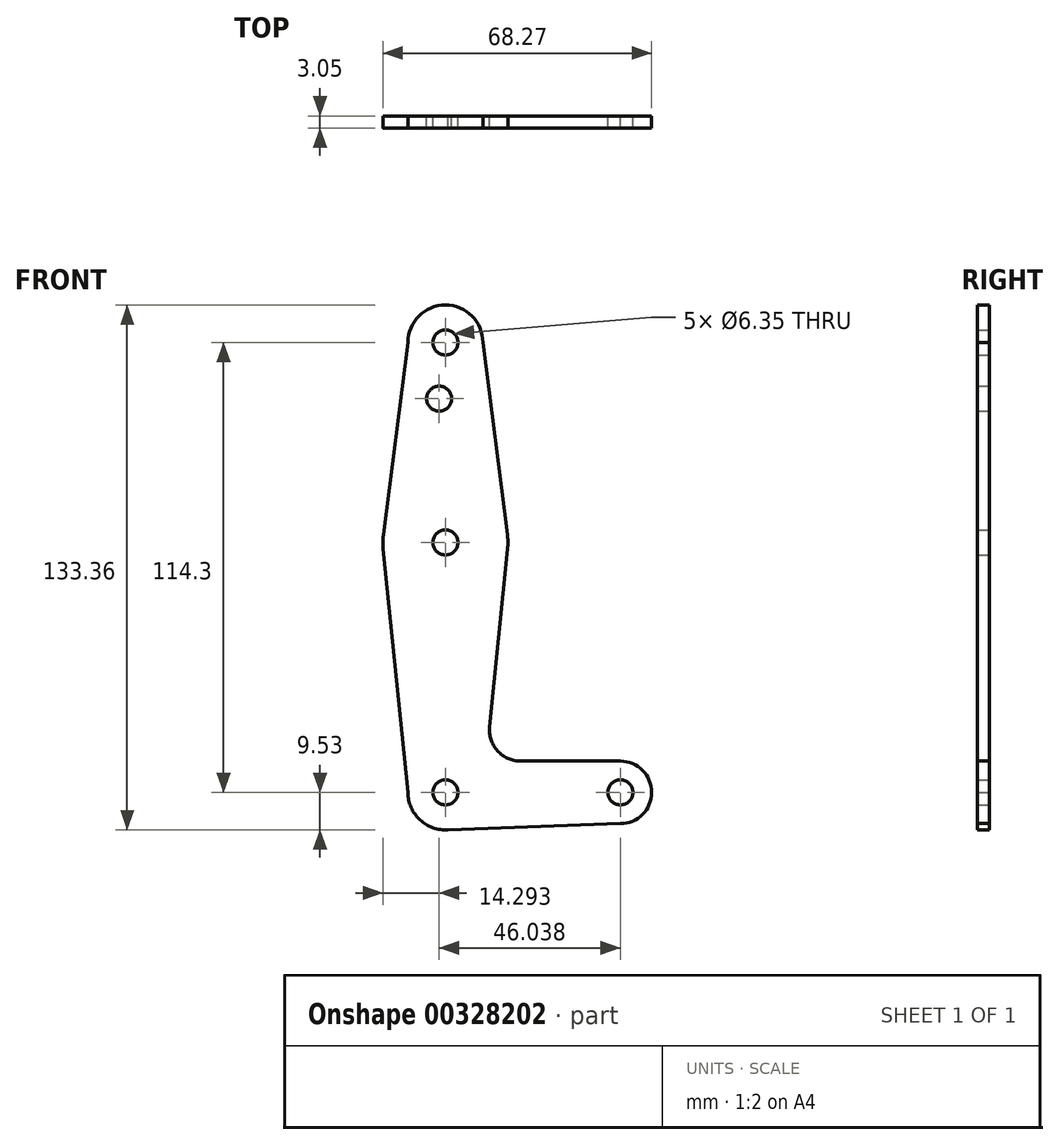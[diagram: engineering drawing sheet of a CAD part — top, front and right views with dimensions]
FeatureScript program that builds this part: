
annotation { "Feature Type Name" : "Feature", "Feature Type Description" : "" }
export const myFeature = defineFeature(function(context is Context, id is Id, definition is map)
    precondition{}
    {
        {
            var Q0;
            Q0=qCreatedBy(makeId("Front.planeOp"),FACE);
            var sketch = newSketch(context, id + "F0", { "sketchPlane" : qUnion([Q0])});
            skLineSegment(sketch, "E0", {"start": v(0, 0) * mm, "end": v(0, 114.3) * mm, "construction": true});
            skCircle(sketch, "E1", {"center": v(0, 114.3) * mm, "radius": 9.53 * mm});
            skCircle(sketch, "E2", {"center": v(0, 63.5) * mm, "radius": 15.88 * mm});
            skCircle(sketch, "E3", {"center": v(0, 0) * mm, "radius": 9.53 * mm});
            skLineSegment(sketch, "E4", {"start": v(0, 0) * mm, "end": v(44.45, 0) * mm, "construction": true});
            skCircle(sketch, "E5", {"center": v(44.45, 0) * mm, "radius": 7.94 * mm});
            skLineSegment(sketch, "E6", {"start": v(0, -9.52) * mm, "end": v(44.45, -7.94) * mm});
            skLineSegment(sketch, "E7", {"start": v(-15.75, 65.5) * mm, "end": v(-9.52, 114.3) * mm});
            skLineSegment(sketch, "E8", {"start": v(15.75, 65.5) * mm, "end": v(9.52, 114.3) * mm});
            skLineSegment(sketch, "E9", {"start": v(-15.8, 61.9) * mm, "end": v(-9.52, 0) * mm});
            skCircle(sketch, "E10", {"center": v(0, 114.3) * mm, "radius": 3.18 * mm});
            skCircle(sketch, "E11", {"center": v(0, 63.5) * mm, "radius": 3.18 * mm});
            skCircle(sketch, "E12", {"center": v(0, 0) * mm, "radius": 3.18 * mm});
            skCircle(sketch, "E13", {"center": v(44.45, 0) * mm, "radius": 3.18 * mm});
            skCircle(sketch, "E14", {"center": v(-1.59, 100.03) * mm, "radius": 3.18 * mm});
            skLineSegment(sketch, "E15", {"start": v(19.12, 7.94) * mm, "end": v(44.45, 7.94) * mm});
            skLineSegment(sketch, "E16", {"start": v(11.22, 16.69) * mm, "end": v(15.8, 61.9) * mm});
            skPoint(sketch, "E17.newPointA", {"position": v(0, 7.94) * mm});
            skPoint(sketch, "E17.newPointB", {"position": v(9.52, 0) * mm});
            skArc(sketch, "E17.filletArc", {"start": v(11.22, 16.69) * mm, "mid": v(13.23, 10.56) * mm, "end": v(19.12, 7.94) * mm});
            skSolve(sketch);
        }
        {
            var Q0;
            Q0 = qSketchRegion(id + "F0", true);
            extrude(context, id + "F1", {"entities" : qUnion([Q0]), "depth" : 3.05 * mm});
        }
    });
